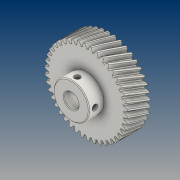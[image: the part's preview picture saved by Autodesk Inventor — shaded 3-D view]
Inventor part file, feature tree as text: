
AUTODESK INVENTOR PART (.ipt)
format: ipt  version: 2021 (Build 250183000, 183)  size: 879,616 bytes
history: native  units: mm (DEFAULTED — no unit token found)
features: extrude x4, sketch x4, plane x3, other x3, chamfer x2, projected_geometry x2, pattern_circular x1
ambient origin geometry x8: Origin, YZ Plane, XZ Plane, XY Plane, X Axis, Y Axis, Z Axis, Center Point
bodies: Solid1 (feature_tree)
feature tree (19):
  extrude  "Extrusion1"  Depth=15.0mm TaperAngle=0.0deg
  plane  "Work Plane2"
  plane  "Work Plane8"
  plane  "Work Plane9"
  other  "Spur Gear"
  sketch  "Sketch3"  dims[d16=45.0mm d17=0.0mm d34=0.747998mm]
  extrude  "Extrusion2"  Depth=10.0mm TaperAngle=0.0deg
  extrude  "Extrusion3"  Depth=0.747998mm TaperAngle=0.0deg
  extrude  "Extrusion4"  TaperAngle=0.0deg  [1 undecoded]
  pattern_circular  "Circular Pattern1"  [2 undecoded]
  chamfer  "Chamfer1"  Distance=45.0mm
  chamfer  "Chamfer2"  [1 undecoded]
  sketch  "Sketch1"  dims[d0=55.253778mm d1=15.0mm d2=0.0mm]
  sketch  "Sketch2"  dims[d3=55.869333mm d4=10.0mm d5=0.0mm]
  other  "Srf1"
  projected_geometry  "Projected Loop1"
  sketch  "Sketch4"  dims[d39=0.0mm d41=0.0mm d43=45.0mm d46=45.0mm d47=0.0mm d48=0.0mm d49=7.0mm d50=9.6mm d51=0.0mm d52=0.0mm d53=10.0mm d54=0.0mm d55=4.0mm d56=3.8mm d57=0.0mm d58=0.0mm d59=20.0mm d60=90.0deg d62=0.5mm d63=2.0mm d64=45.0deg d65=0.5mm d66=2.0mm d67=45.0deg]
  projected_geometry  "Projected Loop2"
  other  "Pitch Diameter"
note: 4 required parameter values undecoded (feature->parameter linkage not recoverable at this tier; creation-order binding heuristic only, values carry confidence <= 0.55)
